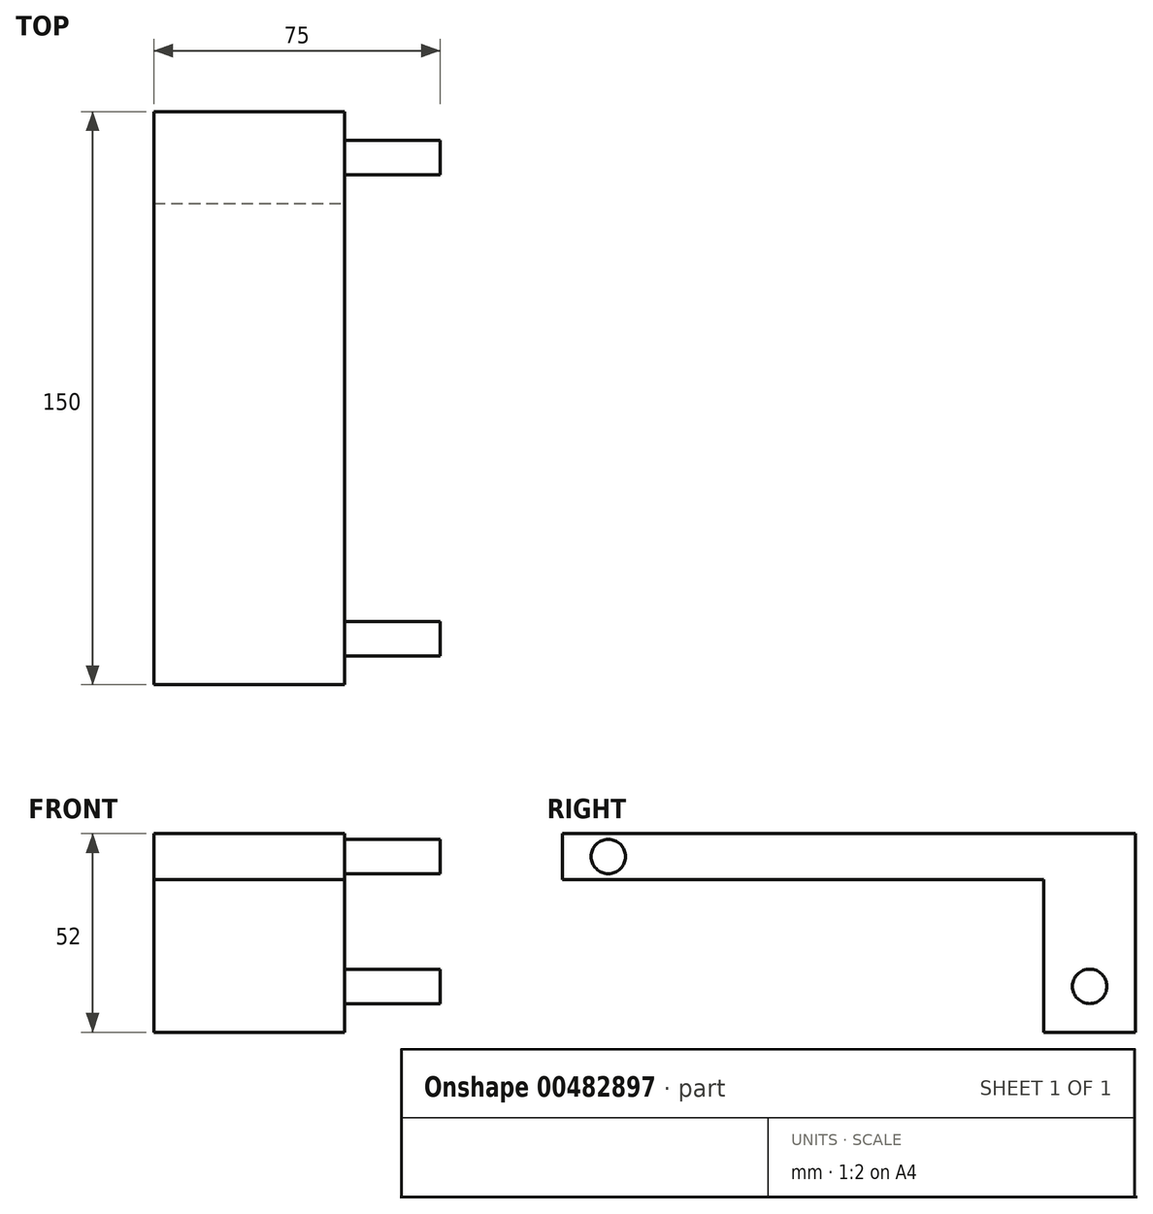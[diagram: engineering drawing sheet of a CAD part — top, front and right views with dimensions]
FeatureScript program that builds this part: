
annotation { "Feature Type Name" : "Feature", "Feature Type Description" : "" }
export const myFeature = defineFeature(function(context is Context, id is Id, definition is map)
    precondition{}
    {
        {
            var Q0;
            Q0=qCreatedBy(makeId("Top.planeOp"),FACE);
            var sketch = newSketch(context, id + "F0", { "sketchPlane" : qUnion([Q0])});
            skLineSegment(sketch, "E0.bottom", {"start": v(25, -75) * mm, "end": v(-25, -75) * mm});
            skLineSegment(sketch, "E0.top", {"start": v(25, 75) * mm, "end": v(-25, 75) * mm});
            skLineSegment(sketch, "E0.left", {"start": v(25, -75) * mm, "end": v(25, 75) * mm});
            skLineSegment(sketch, "E0.right", {"start": v(-25, -75) * mm, "end": v(-25, 75) * mm});
            skPoint(sketch, "E0.middle", {"position": v(0, 0) * mm});
            skSolve(sketch);
        }
        {
            var Q0;
            Q0=makeQuery(id+"F0.imprint","IMPRINT",FACE,{"disambiguationData":[TD([[makeQuery(id+"F0.imprint","IMPRINT",EDGE,{"derivedFrom":sQuery(id+"F0.wireOp",EDGE,"E0.bottom")}),-1.0]])]});
            extrude(context, id + "F1", {"entities" : qUnion([Q0]), "depth" : 12 * mm});
        }
        {
            var Q0;
            Q0=makeQuery(id+"F1.opExtrude","SWEPT_FACE",FACE,{"disambiguationData":[OSD([sQuery(id+"F0.wireOp",EDGE,"E0.left")])]});
            var sketch = newSketch(context, id + "F2", { "sketchPlane" : qUnion([Q0])});
            skLineSegment(sketch, "E1.bottom", {"start": v(75, 0) * mm, "end": v(51, 0) * mm});
            skLineSegment(sketch, "E1.top", {"start": v(75, -40) * mm, "end": v(51, -40) * mm});
            skLineSegment(sketch, "E1.left", {"start": v(75, 0) * mm, "end": v(75, -40) * mm});
            skLineSegment(sketch, "E1.right", {"start": v(51, 0) * mm, "end": v(51, -40) * mm});
            skSolve(sketch);
        }
        {
            var Q0;
            Q0=makeQuery(id+"F2.imprint","IMPRINT",FACE,{"disambiguationData":[TD([[makeQuery(id+"F2.imprint","IMPRINT",EDGE,{"derivedFrom":sQuery(id+"F2.wireOp",EDGE,"E1.bottom")}),-1.0]])]});
            extrude(context, id + "F3", {"entities" : qUnion([Q0]), "operationType" : NewBodyOperationType.ADD, "oppositeDirection" : true, "depth" : 50 * mm});
        }
        {
            var Q0;
            Q0=makeQuery(id+"F1.opExtrude","SWEPT_FACE",FACE,{"disambiguationData":[OSD([sQuery(id+"F0.wireOp",EDGE,"E0.left")])]});
            var sketch = newSketch(context, id + "F4", { "sketchPlane" : qUnion([Q0])});
            skCircle(sketch, "E2", {"center": v(-63, 6) * mm, "radius": 4.5 * mm});
            skPoint(sketch, "E2.centerSnap0", {"position": v(-75, 6) * mm});
            skCircle(sketch, "E3", {"center": v(63, -28) * mm, "radius": 4.5 * mm});
            skPoint(sketch, "E3.centerSnap0", {"position": v(75, -14) * mm});
            skSolve(sketch);
        }
        {
            var Q0;
            Q0=makeQuery(id+"F4.imprint","IMPRINT",FACE,{"disambiguationData":[TD([[makeQuery(id+"F4.imprint","IMPRINT",EDGE,{"derivedFrom":sQuery(id+"F4.wireOp",EDGE,"E2")}),1.0]])]});
            var Q1;
            Q1=makeQuery(id+"F4.imprint","IMPRINT",FACE,{"disambiguationData":[TD([[makeQuery(id+"F4.imprint","IMPRINT",EDGE,{"derivedFrom":sQuery(id+"F4.wireOp",EDGE,"E3")}),1.0]])]});
            extrude(context, id + "F5", {"entities" : qUnion([Q0, Q1]), "operationType" : NewBodyOperationType.ADD, "depth" : 25 * mm});
        }
    });
